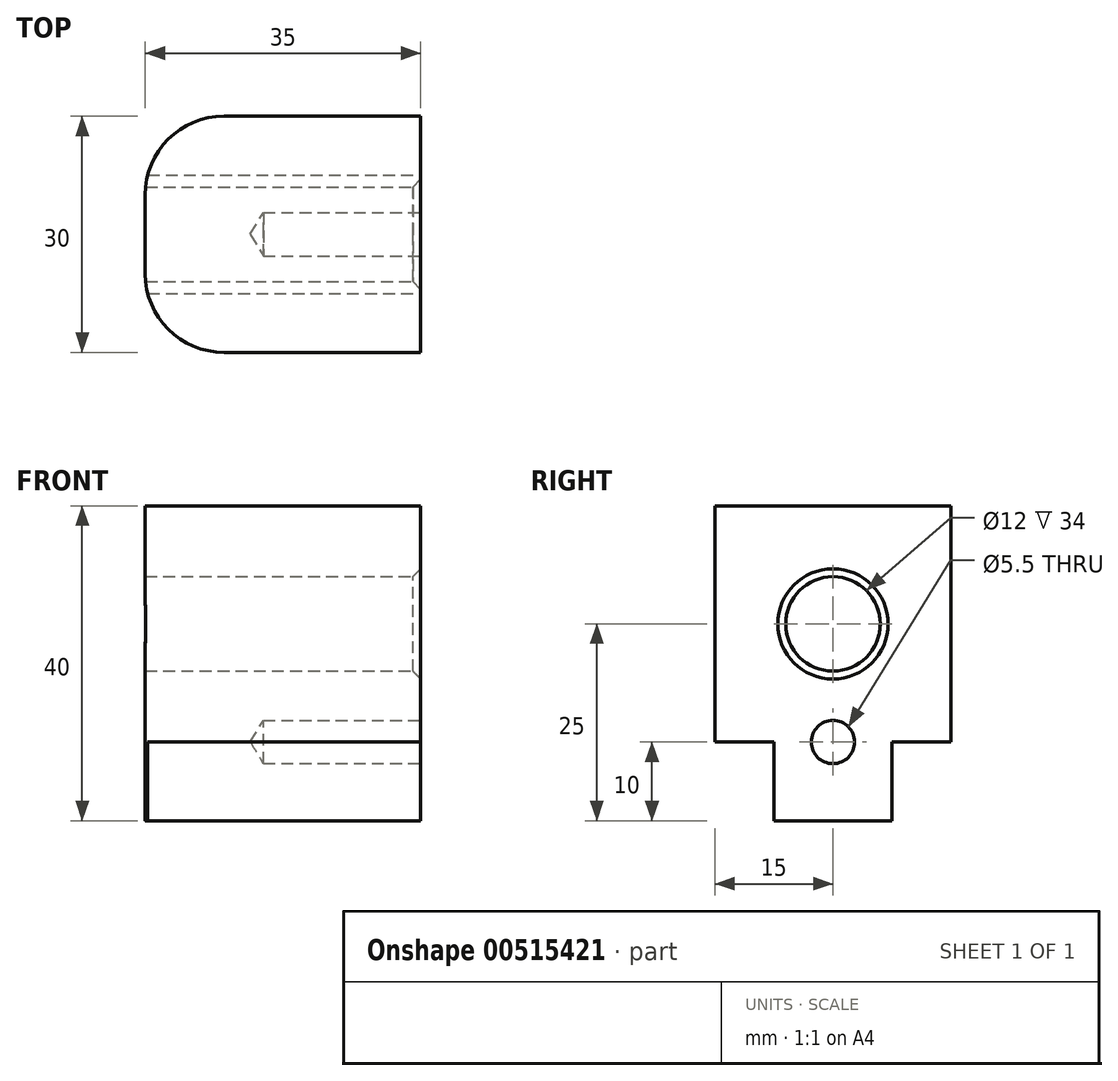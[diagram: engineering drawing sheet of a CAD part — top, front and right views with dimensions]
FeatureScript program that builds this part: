
annotation { "Feature Type Name" : "Feature", "Feature Type Description" : "" }
export const myFeature = defineFeature(function(context is Context, id is Id, definition is map)
    precondition{}
    {
        {
            var Q0;
            Q0=qCreatedBy(makeId("Right.planeOp"),FACE);
            var sketch = newSketch(context, id + "F0", { "sketchPlane" : qUnion([Q0])});
            skLineSegment(sketch, "E0", {"start": v(0, 30) * mm, "end": v(15, 30) * mm});
            skLineSegment(sketch, "E1", {"start": v(15, 30) * mm, "end": v(15, 0) * mm});
            skLineSegment(sketch, "E2", {"start": v(15, 0) * mm, "end": v(7.5, 0) * mm});
            skLineSegment(sketch, "E3", {"start": v(7.5, 0) * mm, "end": v(7.5, -10) * mm});
            skLineSegment(sketch, "E4", {"start": v(7.5, -10) * mm, "end": v(0, -10) * mm});
            skLineSegment(sketch, "E5", {"start": v(0, 30) * mm, "end": v(0, -10) * mm, "construction": true});
            skLineSegment(sketch, "E6.MirrorCS", {"start": v(0, 30) * mm, "end": v(-15, 30) * mm});
            skLineSegment(sketch, "E7.MirrorCS", {"start": v(-15, 30) * mm, "end": v(-15, 0) * mm});
            skLineSegment(sketch, "E8.MirrorCS", {"start": v(-15, 0) * mm, "end": v(-7.5, 0) * mm});
            skLineSegment(sketch, "E9.MirrorCS", {"start": v(-7.5, 0) * mm, "end": v(-7.5, -10) * mm});
            skLineSegment(sketch, "E10.MirrorCS", {"start": v(-7.5, -10) * mm, "end": v(0, -10) * mm});
            skPoint(sketch, "E11", {"position": v(0, 0) * mm});
            skSolve(sketch);
        }
        {
            var Q0;
            Q0=makeQuery(id+"F0.imprint","IMPRINT",FACE,{"disambiguationData":[TD([[makeQuery(id+"F0.imprint","IMPRINT",EDGE,{"derivedFrom":sQuery(id+"F0.wireOp",EDGE,"E0")}),-1.0]])]});
            extrude(context, id + "F1", {"entities" : qUnion([Q0]), "oppositeDirection" : true, "depth" : 35 * mm, "offsetDistance" : 25 * mm});
        }
        {
            var Q0;
            Q0=makeQuery(id+"F1.opExtrude","CAP_FACE",FACE,{"disambiguationData":[OSD([sQuery(id+"F0.wireOp",EDGE,"E0"),sQuery(id+"F0.wireOp",EDGE,"E1"),sQuery(id+"F0.wireOp",EDGE,"E2"),sQuery(id+"F0.wireOp",EDGE,"E3"),sQuery(id+"F0.wireOp",EDGE,"E4"),sQuery(id+"F0.wireOp",EDGE,"E6.MirrorCS"),sQuery(id+"F0.wireOp",EDGE,"E7.MirrorCS"),sQuery(id+"F0.wireOp",EDGE,"E8.MirrorCS"),sQuery(id+"F0.wireOp",EDGE,"E9.MirrorCS"),sQuery(id+"F0.wireOp",EDGE,"E10.MirrorCS")])],"isStart":true});
            var sketch = newSketch(context, id + "F2", { "sketchPlane" : qUnion([Q0])});
            skPoint(sketch, "E12", {"position": v(0, 15) * mm});
            skPoint(sketch, "E12.positionSnap0", {"position": v(-15, 15) * mm});
            skSolve(sketch);
        }
        {
            var Q0;
            Q0=sQuery(id+"F2.wireOp",VERTEX,"E12");
            var Q1;
            Q1=makeQuery(id+"F1.opExtrude","SWEPT_BODY",BODY,{"disambiguationData":[OSD([sQuery(id+"F0.wireOp",EDGE,"E0"),sQuery(id+"F0.wireOp",EDGE,"E1"),sQuery(id+"F0.wireOp",EDGE,"E2"),sQuery(id+"F0.wireOp",EDGE,"E3"),sQuery(id+"F0.wireOp",EDGE,"E4"),sQuery(id+"F0.wireOp",EDGE,"E6.MirrorCS"),sQuery(id+"F0.wireOp",EDGE,"E7.MirrorCS"),sQuery(id+"F0.wireOp",EDGE,"E8.MirrorCS"),sQuery(id+"F0.wireOp",EDGE,"E9.MirrorCS"),sQuery(id+"F0.wireOp",EDGE,"E10.MirrorCS")])]});
            hole(context, id + "F3", {"style" : HoleStyle.C_SINK, "endStyle" : HoleEndStyle.THROUGH, "holeDiameter" : 12 * mm, "cSinkDiameter" : 14 * mm, "cSinkAngle" : 90 * degree, "isTappedThrough" : true, "tappedDepth" : 12 * mm, "tapClearance" : 3, "locations" : qUnion([Q0]), "scope" : qUnion([Q1])});
        }
        {
            var Q0;
            Q0=makeQuery(id+"F1.opExtrude","CAP_EDGE",EDGE,{"disambiguationData":[OSD([sQuery(id+"F0.wireOp",EDGE,"E1")])],"isStart":false});
            var Q1;
            Q1=makeQuery(id+"F1.opExtrude","CAP_EDGE",EDGE,{"disambiguationData":[OSD([sQuery(id+"F0.wireOp",EDGE,"E7.MirrorCS")])],"isStart":false});
            fillet(context, id + "F4", {"entities" : qUnion([Q0, Q1]), "radius" : 10 * mm, "tangentPropagation" : true, "allowEdgeOverflow" : false});
        }
        {
            var Q0;
            Q0=sQuery(id+"F0.wireOp",VERTEX,"E11");
            var Q1;
            Q1=makeQuery(id+"F1.opExtrude","SWEPT_BODY",BODY,{"disambiguationData":[OSD([sQuery(id+"F0.wireOp",EDGE,"E0"),sQuery(id+"F0.wireOp",EDGE,"E1"),sQuery(id+"F0.wireOp",EDGE,"E2"),sQuery(id+"F0.wireOp",EDGE,"E3"),sQuery(id+"F0.wireOp",EDGE,"E4"),sQuery(id+"F0.wireOp",EDGE,"E6.MirrorCS"),sQuery(id+"F0.wireOp",EDGE,"E7.MirrorCS"),sQuery(id+"F0.wireOp",EDGE,"E8.MirrorCS"),sQuery(id+"F0.wireOp",EDGE,"E9.MirrorCS"),sQuery(id+"F0.wireOp",EDGE,"E10.MirrorCS")])]});
            hole(context, id + "F5", {"style" : HoleStyle.SIMPLE, "endStyle" : HoleEndStyle.BLIND, "standardTappedOrClearance" : lookupTablePath({ "standard" : "ISO", "fit" : "Normal", "size" : "M5", "type" : "Clearance" }), "standardBlindInLast" : lookupTablePath({ "fit" : "Standard", "standard" : "ISO", "size" : "M5", "type" : "Clearance" }), "holeDiameter" : 5.5 * mm, "holeDepth" : 20 * mm, "isTappedThrough" : true, "tappedDepth" : 12 * mm, "tapClearance" : 3, "locations" : qUnion([Q0]), "scope" : qUnion([Q1])});
        }
    });
